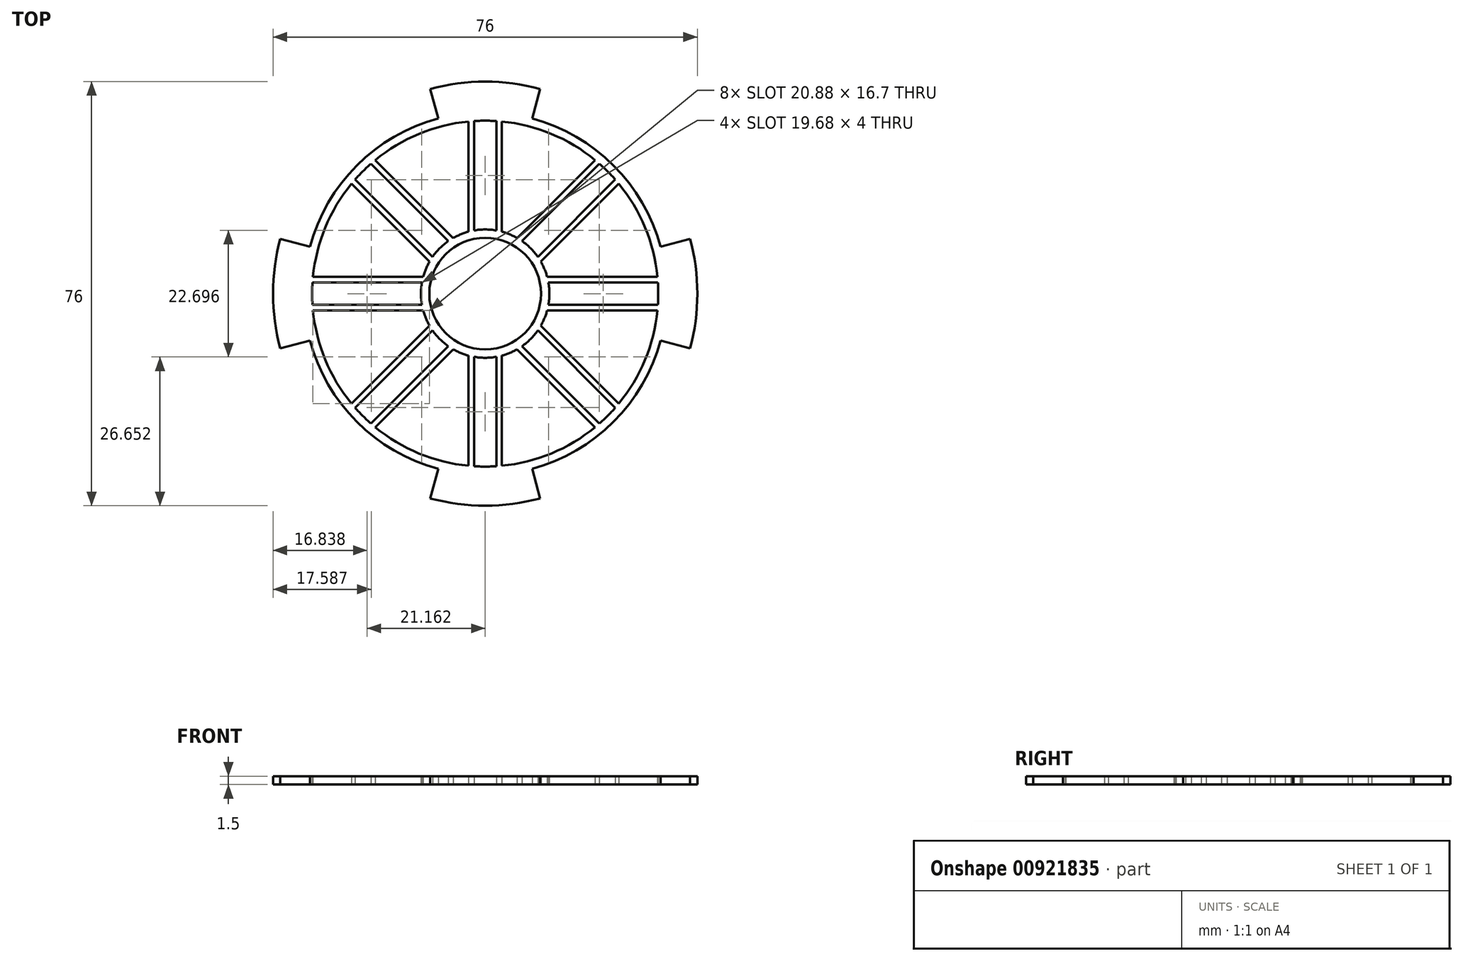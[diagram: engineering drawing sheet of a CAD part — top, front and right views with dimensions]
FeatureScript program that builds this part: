
annotation { "Feature Type Name" : "Feature", "Feature Type Description" : "" }
export const myFeature = defineFeature(function(context is Context, id is Id, definition is map)
    precondition{}
    {
        {
            var Q0;
            Q0=qCreatedBy(makeId("Top.planeOp"),FACE);
            var sketch = newSketch(context, id + "F0", { "sketchPlane" : qUnion([Q0])});
            skArc(sketch, "E0", {"start": v(-36.7, 9.84) * mm, "mid": v(-38, 0) * mm, "end": v(-36.7, -9.84) * mm});
            skArc(sketch, "E1", {"start": v(-8.41, 31.4) * mm, "mid": v(-22.98, 22.98) * mm, "end": v(-31.4, 8.41) * mm});
            skCircle(sketch, "E2", {"center": v(0, 0) * mm, "radius": 10 * mm});
            skArc(sketch, "E3", {"start": v(-3, 30.85) * mm, "mid": v(-11.86, 28.64) * mm, "end": v(-19.7, 23.94) * mm});
            skArc(sketch, "E4", {"start": v(2, 11.32) * mm, "mid": v(0, 11.5) * mm, "end": v(-2, 11.32) * mm});
            skLineSegment(sketch, "E5.trimOffspring", {"start": v(-8.41, 31.4) * mm, "end": v(-9.84, 36.7) * mm});
            skLineSegment(sketch, "E6.trimOffspring", {"start": v(8.41, 31.4) * mm, "end": v(9.84, 36.7) * mm});
            skLineSegment(sketch, "E7.1.0", {"start": v(-31.4, 8.41) * mm, "end": v(-36.7, 9.84) * mm});
            skLineSegment(sketch, "E7.1.1", {"start": v(-31.4, -8.41) * mm, "end": v(-36.7, -9.84) * mm});
            skLineSegment(sketch, "E7.2.0", {"start": v(-8.41, -31.4) * mm, "end": v(-9.84, -36.7) * mm});
            skLineSegment(sketch, "E7.2.1", {"start": v(8.41, -31.4) * mm, "end": v(9.84, -36.7) * mm});
            skLineSegment(sketch, "E7.3.0", {"start": v(31.4, -8.41) * mm, "end": v(36.7, -9.84) * mm});
            skLineSegment(sketch, "E7.3.1", {"start": v(31.4, 8.41) * mm, "end": v(36.7, 9.84) * mm});
            skArc(sketch, "E8.trimOffspring", {"start": v(9.84, 36.7) * mm, "mid": v(0, 38) * mm, "end": v(-9.84, 36.7) * mm});
            skArc(sketch, "E9.trimOffspring", {"start": v(36.7, -9.84) * mm, "mid": v(38, 0) * mm, "end": v(36.7, 9.84) * mm});
            skArc(sketch, "E10.trimOffspring", {"start": v(-9.84, -36.7) * mm, "mid": v(0, -38) * mm, "end": v(9.84, -36.7) * mm});
            skArc(sketch, "E11.trimOffspring", {"start": v(-31.4, -8.41) * mm, "mid": v(-22.98, -22.98) * mm, "end": v(-8.41, -31.4) * mm});
            skArc(sketch, "E12.trimOffspring", {"start": v(31.4, 8.41) * mm, "mid": v(22.98, 22.98) * mm, "end": v(8.41, 31.4) * mm});
            skArc(sketch, "E13.trimOffspring", {"start": v(8.41, -31.4) * mm, "mid": v(22.98, -22.98) * mm, "end": v(31.4, -8.41) * mm});
            skLineSegment(sketch, "E14", {"start": v(-3, 30.85) * mm, "end": v(-3, 11.1) * mm});
            skLineSegment(sketch, "E15", {"start": v(-2, 30.94) * mm, "end": v(-2, 11.32) * mm});
            skLineSegment(sketch, "E16.MirrorCS", {"start": v(2, 30.94) * mm, "end": v(2, 11.32) * mm});
            skLineSegment(sketch, "E17.MirrorCS", {"start": v(3, 30.85) * mm, "end": v(3, 11.1) * mm});
            skArc(sketch, "E18.trimOffspring", {"start": v(2, 30.94) * mm, "mid": v(0, 31) * mm, "end": v(-2, 30.94) * mm});
            skArc(sketch, "E19.trimOffspring", {"start": v(-3, 11.1) * mm, "mid": v(-4.4, 10.62) * mm, "end": v(-5.73, 9.97) * mm});
            skLineSegment(sketch, "E20.1.0", {"start": v(-30.85, 3) * mm, "end": v(-11.1, 3) * mm});
            skLineSegment(sketch, "E20.1.1", {"start": v(-30.94, 2) * mm, "end": v(-11.32, 2) * mm});
            skLineSegment(sketch, "E20.1.2", {"start": v(-30.94, -2) * mm, "end": v(-11.32, -2) * mm});
            skLineSegment(sketch, "E20.1.3", {"start": v(-30.85, -3) * mm, "end": v(-11.1, -3) * mm});
            skLineSegment(sketch, "E20.2.0", {"start": v(-3, -30.85) * mm, "end": v(-3, -11.1) * mm});
            skLineSegment(sketch, "E20.2.1", {"start": v(-2, -30.94) * mm, "end": v(-2, -11.32) * mm});
            skLineSegment(sketch, "E20.2.2", {"start": v(2, -30.94) * mm, "end": v(2, -11.32) * mm});
            skLineSegment(sketch, "E20.2.3", {"start": v(3, -30.85) * mm, "end": v(3, -11.1) * mm});
            skLineSegment(sketch, "E20.3.0", {"start": v(30.85, -3) * mm, "end": v(11.1, -3) * mm});
            skLineSegment(sketch, "E20.3.1", {"start": v(30.94, -2) * mm, "end": v(11.32, -2) * mm});
            skLineSegment(sketch, "E20.3.2", {"start": v(30.94, 2) * mm, "end": v(11.32, 2) * mm});
            skLineSegment(sketch, "E20.3.3", {"start": v(30.85, 3) * mm, "end": v(11.1, 3) * mm});
            skArc(sketch, "E21.trimOffspring", {"start": v(30.85, 3) * mm, "mid": v(28.64, 11.86) * mm, "end": v(23.94, 19.7) * mm});
            skArc(sketch, "E22.trimOffspring", {"start": v(30.94, -2) * mm, "mid": v(31, 0) * mm, "end": v(30.94, 2) * mm});
            skArc(sketch, "E23.trimOffspring", {"start": v(11.1, 3) * mm, "mid": v(10.62, 4.4) * mm, "end": v(9.97, 5.73) * mm});
            skArc(sketch, "E24.trimOffspring", {"start": v(11.32, -2) * mm, "mid": v(11.5, 0) * mm, "end": v(11.32, 2) * mm});
            skArc(sketch, "E25.trimOffspring", {"start": v(3, -11.1) * mm, "mid": v(4.4, -10.62) * mm, "end": v(5.73, -9.97) * mm});
            skArc(sketch, "E26.trimOffspring", {"start": v(-2, -11.32) * mm, "mid": v(0, -11.5) * mm, "end": v(2, -11.32) * mm});
            skArc(sketch, "E27.trimOffspring", {"start": v(-2, -30.94) * mm, "mid": v(0, -31) * mm, "end": v(2, -30.94) * mm});
            skArc(sketch, "E28.trimOffspring", {"start": v(3, -30.85) * mm, "mid": v(11.86, -28.64) * mm, "end": v(19.7, -23.94) * mm});
            skArc(sketch, "E29.trimOffspring", {"start": v(-11.32, 2) * mm, "mid": v(-11.5, 0) * mm, "end": v(-11.32, -2) * mm});
            skArc(sketch, "E30.trimOffspring", {"start": v(-11.1, -3) * mm, "mid": v(-10.62, -4.4) * mm, "end": v(-9.97, -5.73) * mm});
            skArc(sketch, "E31.trimOffspring", {"start": v(-30.94, 2) * mm, "mid": v(-31, 0) * mm, "end": v(-30.94, -2) * mm});
            skArc(sketch, "E32.trimOffspring", {"start": v(-30.85, -3) * mm, "mid": v(-28.64, -11.86) * mm, "end": v(-23.94, -19.7) * mm});
            skLineSegment(sketch, "E33", {"start": v(0, 0) * mm, "end": v(-25.69, 25.69) * mm, "construction": true});
            skLineSegment(sketch, "E34", {"start": v(-19.7, 23.94) * mm, "end": v(-5.73, 9.97) * mm});
            skLineSegment(sketch, "E35", {"start": v(-20.46, 23.29) * mm, "end": v(-6.6, 9.42) * mm});
            skLineSegment(sketch, "E36.MirrorCS", {"start": v(-23.29, 20.46) * mm, "end": v(-9.42, 6.6) * mm});
            skLineSegment(sketch, "E37.MirrorCS", {"start": v(-23.94, 19.7) * mm, "end": v(-9.97, 5.73) * mm});
            skArc(sketch, "E38.trimOffspring", {"start": v(-20.46, 23.29) * mm, "mid": v(-21.92, 21.92) * mm, "end": v(-23.29, 20.46) * mm});
            skArc(sketch, "E39.trimOffspring", {"start": v(-23.94, 19.7) * mm, "mid": v(-28.64, 11.86) * mm, "end": v(-30.85, 3) * mm});
            skArc(sketch, "E40.trimOffspring", {"start": v(-6.6, 9.42) * mm, "mid": v(-8.13, 8.13) * mm, "end": v(-9.42, 6.6) * mm});
            skArc(sketch, "E41.trimOffspring", {"start": v(-9.97, 5.73) * mm, "mid": v(-10.62, 4.4) * mm, "end": v(-11.1, 3) * mm});
            skLineSegment(sketch, "E42.1.0", {"start": v(-23.94, -19.7) * mm, "end": v(-9.97, -5.73) * mm});
            skLineSegment(sketch, "E42.1.1", {"start": v(-23.29, -20.46) * mm, "end": v(-9.42, -6.6) * mm});
            skLineSegment(sketch, "E42.1.2", {"start": v(-20.46, -23.29) * mm, "end": v(-6.6, -9.42) * mm});
            skLineSegment(sketch, "E42.1.3", {"start": v(-19.7, -23.94) * mm, "end": v(-5.73, -9.97) * mm});
            skLineSegment(sketch, "E42.2.0", {"start": v(19.7, -23.94) * mm, "end": v(5.73, -9.97) * mm});
            skLineSegment(sketch, "E42.2.1", {"start": v(20.46, -23.29) * mm, "end": v(6.6, -9.42) * mm});
            skLineSegment(sketch, "E42.2.2", {"start": v(23.29, -20.46) * mm, "end": v(9.42, -6.6) * mm});
            skLineSegment(sketch, "E42.2.3", {"start": v(23.94, -19.7) * mm, "end": v(9.97, -5.73) * mm});
            skLineSegment(sketch, "E42.3.0", {"start": v(23.94, 19.7) * mm, "end": v(9.97, 5.73) * mm});
            skLineSegment(sketch, "E42.3.1", {"start": v(23.29, 20.46) * mm, "end": v(9.42, 6.6) * mm});
            skLineSegment(sketch, "E42.3.2", {"start": v(20.46, 23.29) * mm, "end": v(6.6, 9.42) * mm});
            skLineSegment(sketch, "E42.3.3", {"start": v(19.7, 23.94) * mm, "end": v(5.73, 9.97) * mm});
            skArc(sketch, "E43.trimOffspring", {"start": v(5.73, 9.97) * mm, "mid": v(4.4, 10.62) * mm, "end": v(3, 11.1) * mm});
            skArc(sketch, "E44.trimOffspring", {"start": v(19.7, 23.94) * mm, "mid": v(11.86, 28.64) * mm, "end": v(3, 30.85) * mm});
            skArc(sketch, "E45.trimOffspring", {"start": v(23.29, 20.46) * mm, "mid": v(21.92, 21.92) * mm, "end": v(20.46, 23.29) * mm});
            skArc(sketch, "E46.trimOffspring", {"start": v(9.42, 6.6) * mm, "mid": v(8.13, 8.13) * mm, "end": v(6.6, 9.42) * mm});
            skArc(sketch, "E47.trimOffspring", {"start": v(9.97, -5.73) * mm, "mid": v(10.62, -4.4) * mm, "end": v(11.1, -3) * mm});
            skArc(sketch, "E48.trimOffspring", {"start": v(6.6, -9.42) * mm, "mid": v(8.13, -8.13) * mm, "end": v(9.42, -6.6) * mm});
            skArc(sketch, "E49.trimOffspring", {"start": v(-5.73, -9.97) * mm, "mid": v(-4.4, -10.62) * mm, "end": v(-3, -11.1) * mm});
            skArc(sketch, "E50.trimOffspring", {"start": v(-9.42, -6.6) * mm, "mid": v(-8.13, -8.13) * mm, "end": v(-6.6, -9.42) * mm});
            skArc(sketch, "E51.trimOffspring", {"start": v(-19.7, -23.94) * mm, "mid": v(-11.86, -28.64) * mm, "end": v(-3, -30.85) * mm});
            skArc(sketch, "E52.trimOffspring", {"start": v(-23.29, -20.46) * mm, "mid": v(-21.92, -21.92) * mm, "end": v(-20.46, -23.29) * mm});
            skArc(sketch, "E53.trimOffspring", {"start": v(23.94, -19.7) * mm, "mid": v(28.64, -11.86) * mm, "end": v(30.85, -3) * mm});
            skArc(sketch, "E54.trimOffspring", {"start": v(20.46, -23.29) * mm, "mid": v(21.92, -21.92) * mm, "end": v(23.29, -20.46) * mm});
            skSolve(sketch);
        }
        {
            var Q0;
            Q0 = qSketchRegion(id + "F0", true);
            extrude(context, id + "F1", {"entities" : qUnion([Q0]), "depth" : 1.5 * mm, "offsetDistance" : 25 * mm});
        }
    });
